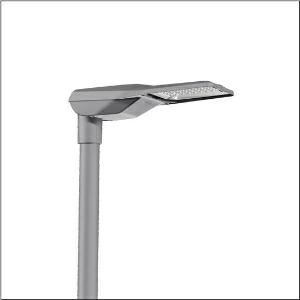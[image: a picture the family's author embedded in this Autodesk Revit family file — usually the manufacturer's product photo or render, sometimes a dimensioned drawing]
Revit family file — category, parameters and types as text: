
# Revit family: streetlight_sl_21_iq_mini___st0_5a_5xe2b41g08jb_20f7
name_source: partatom
category: Lighting Fixtures
units: mm (PartAtom-declared; Revit-internal decimal feet)

## family parameters
Cut with Voids When Loaded = No
Host = Face
Light Source = No
Part Type = Normal
Room Calculation Point = No
Round Connector Dimension = Use Diameter
Shared = No

## types (1)
- --- (1 x LED, 11290 lm, 71.6 W, 4000K)
    Apparent Load = 72 VA
    CIE Flux Codes = 43 76 97 100 100
    Color Rendering = 70
    Color Temperature = 4000K
    Default Elevation = 1800 mm
    Description = Streetlight SL 21 iQ mini, mast luminaire, primary light control with lens, of PMMA, primary optical cover: cover, of toughened safety glass, transparent, light distribution: ST0.5a, light emission: direct distribution, primary light characteristic: asymmetric, installation type: post-top, side-entry, LED, High Power LED, rated luminous flux: 11.290lm, luminous efficacy: 158lm/W, light colour: 740, colour temperature: 4000K, control: Street-Remote, Auto-Match, Temp-Guard, Lumen-Switch, Night-Set, Smart-Wire, Light-Fading, Desk-Remote (wireless, voltage-free reading and setting of iQ features in the workshop via application-optimized NFC function/RFID function), optimised constant luminous flux control (CLO 2.0), presetting dimming linear, mains connection: 220..240V, AC, 50/60Hz, start of lifetime: 72W, end of service life: 75W, reduction: 33W, luminaire housing, of diecast aluminium, powder-coated, Siteco® metallic grey (DB 702S), corrosivity category C5 mid according to DIN EN ISO 12944, please order mast flange separately, inclination adjustable: 0°, 5°, 10°, 15°, sealing non-destructively replaceable, multi-level sealing system, length: 628mm, width: 235mm, height: 110mm, mast flange for spigot size: 42mm (side-entry): 5XC10008XM4, 60/48mm (side-entry/post-top): 5XC10108XM2, 76/60mm (side-entry/post-top): 5XC10108XM1, protection rating (complete): IP66, insulation class (complete): insulation class II (safety insulation), certification: CE, ENEC, ENEC+, VDE, impact resistance: IK09, permissible operating ambient temperature for outdoor applications: -40..+50°C, standard-compliant lighting for roads and squares, packaging unit: 1 piece

Light Distribution: ST0.5a
    Height = 110 mm
    Lamp = 1 x LED
    Lamp Light Flux = 11290 lm
    Lamp Power = 71.6 W
    Lamp count = 1
    Length = 625 mm
    Luminous efficacy = 158 lm/W
    Manufacturer = Siteco
    ModVariant = No
    Model = 5XE2B41G08JB
    Number of Poles = 1
    OnlyDefault = Yes
    Power Factor = 1
    Product Name = Streetlight SL 21 iQ mini | ST0.5a
    Product group = mast luminaire | pylon top
    ProductGroupID = 6100
    Protection Class = Protection class II
    Protection Degree = IP 66
    RLX_Detail_Level = 1
    RLX_Emergency_Light_Flux = 0 lm
    RLX_Emergency_Type = 0
    RLX_Emergency_Type_DB = No
    RlxData = <blob elided: 103633 chars, md5=5df9cfd0>
    Socket = socket
    Standby Power = 0 W
    System Light Flux = 11290 lm
    System Power = 72 W
    Type Comments = factory setting: luminous flux: 100 % | dim-lin: 254 | 746 mA
    Type Image = l_1003519.jpg
    URL = http://relux.com
    VarID = @adj_122629
    Voltage = 0 V
    Weight = 0.00 kg
    Width = 234 mm

## geometry (parser evidence)
native form markers: Blend x4, Sweep x9
no freeform markers — native parametric forms only
